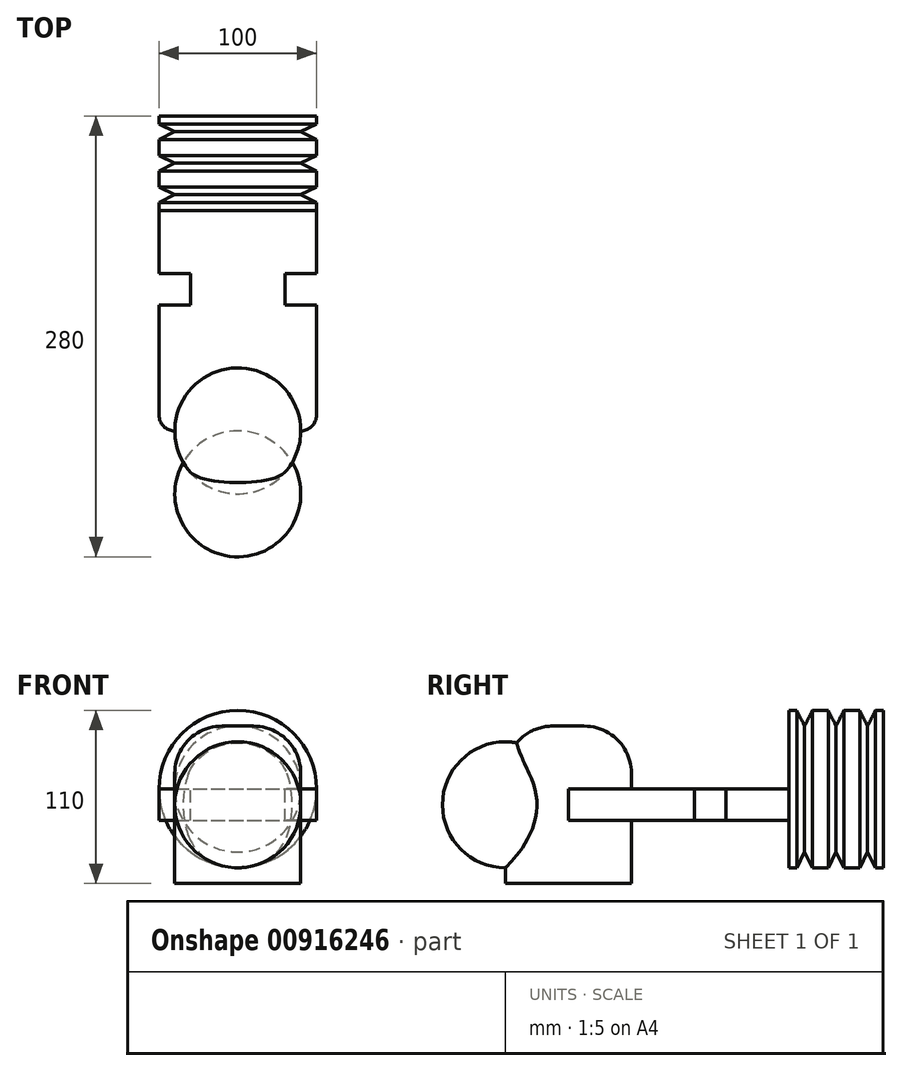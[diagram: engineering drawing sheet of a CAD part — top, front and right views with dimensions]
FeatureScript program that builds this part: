
annotation { "Feature Type Name" : "Feature", "Feature Type Description" : "" }
export const myFeature = defineFeature(function(context is Context, id is Id, definition is map)
    precondition{}
    {
        {
            var Q0;
            Q0=qCreatedBy(makeId("Front.planeOp"),FACE);
            var sketch = newSketch(context, id + "F0", { "sketchPlane" : qUnion([Q0])});
            skLineSegment(sketch, "E0.bottom", {"start": v(50, 10) * mm, "end": v(-50, 10) * mm});
            skLineSegment(sketch, "E0.top", {"start": v(50, -10) * mm, "end": v(-50, -10) * mm});
            skLineSegment(sketch, "E0.left", {"start": v(50, 10) * mm, "end": v(50, -10) * mm});
            skLineSegment(sketch, "E0.right", {"start": v(-50, 10) * mm, "end": v(-50, -10) * mm});
            skPoint(sketch, "E0.middle", {"position": v(0, 0) * mm});
            skSolve(sketch);
        }
        {
            var Q0;
            Q0 = qSketchRegion(id + "F0", true);
            extrude(context, id + "F1", {"entities" : qUnion([Q0]), "endBound" : BoundingType.SYMMETRIC, "depth" : 200 * mm, "offsetDistance" : 25 * mm});
        }
        {
            var Q0;
            Q0=makeQuery(id+"F1.opExtrude","SWEPT_FACE",FACE,{"disambiguationData":[OSD([sQuery(id+"F0.wireOp",EDGE,"E0.bottom")])]});
            var sketch = newSketch(context, id + "F2", { "sketchPlane" : qUnion([Q0])});
            skLineSegment(sketch, "E1.bottom", {"start": v(50, 0) * mm, "end": v(30, 0) * mm});
            skLineSegment(sketch, "E1.top", {"start": v(50, -20) * mm, "end": v(30, -20) * mm});
            skLineSegment(sketch, "E1.left", {"start": v(50, 0) * mm, "end": v(50, -20) * mm});
            skLineSegment(sketch, "E1.right", {"start": v(30, 0) * mm, "end": v(30, -20) * mm});
            skLineSegment(sketch, "E2.MirrorCS", {"start": v(-30, 0) * mm, "end": v(-30, -20) * mm});
            skLineSegment(sketch, "E3.MirrorCS", {"start": v(-50, 0) * mm, "end": v(-30, 0) * mm});
            skLineSegment(sketch, "E4.MirrorCS", {"start": v(-50, -20) * mm, "end": v(-30, -20) * mm});
            skLineSegment(sketch, "E5.MirrorCS", {"start": v(-50, 0) * mm, "end": v(-50, -20) * mm});
            skSolve(sketch);
        }
        {
            var Q0;
            Q0 = qSketchRegion(id + "F2", true);
            extrude(context, id + "F3", {"entities" : qUnion([Q0]), "operationType" : NewBodyOperationType.REMOVE, "oppositeDirection" : true, "depth" : 20 * mm, "offsetDistance" : 25 * mm});
        }
        {
            var Q0;
            Q0=makeQuery(id+"F1.opExtrude","SWEPT_FACE",FACE,{"disambiguationData":[OSD([sQuery(id+"F0.wireOp",EDGE,"E0.bottom")])]});
            var sketch = newSketch(context, id + "F4", { "sketchPlane" : qUnion([Q0])});
            skLineSegment(sketch, "E6", {"start": v(50, 90) * mm, "end": v(40, 90) * mm, "construction": true});
            skLineSegment(sketch, "E7", {"start": v(40, 90) * mm, "end": v(50, 95) * mm});
            skLineSegment(sketch, "E8.MirrorCS", {"start": v(40, 90) * mm, "end": v(50, 85) * mm});
            skLineSegment(sketch, "E9.1.0.0", {"start": v(40, 70) * mm, "end": v(50, 75) * mm});
            skLineSegment(sketch, "E9.1.0.1", {"start": v(40, 70) * mm, "end": v(50, 65) * mm});
            skLineSegment(sketch, "E9.2.0.0", {"start": v(40, 50) * mm, "end": v(50, 55) * mm});
            skLineSegment(sketch, "E9.2.0.1", {"start": v(40, 50) * mm, "end": v(50, 45) * mm});
            skLineSegment(sketch, "E9.direction1", {"start": v(40, 90) * mm, "end": v(40, 70) * mm, "construction": true});
            skLineSegment(sketch, "E10", {"start": v(50, 95) * mm, "end": v(50, 100) * mm});
            skLineSegment(sketch, "E11", {"start": v(50, 100) * mm, "end": v(0, 100) * mm});
            skLineSegment(sketch, "E12", {"start": v(0, 100) * mm, "end": v(0, 40) * mm});
            skLineSegment(sketch, "E13", {"start": v(0, 40) * mm, "end": v(50, 40) * mm});
            skLineSegment(sketch, "E14", {"start": v(50, 40) * mm, "end": v(50, 45) * mm});
            skLineSegment(sketch, "E15.trimOffspring", {"start": v(50, 75) * mm, "end": v(50, 85) * mm});
            skLineSegment(sketch, "E16.trimOffspring", {"start": v(50, 55) * mm, "end": v(50, 65) * mm});
            skSolve(sketch);
        }
        {
            var Q0;
            Q0 = qSketchRegion(id + "F4", true);
            var Q1;
            Q1=sQuery(id+"F4.wireOp",EDGE,"E12");
            revolve(context, id + "F5", {"surfaceOperationType" : NewSurfaceOperationType.NEW, "entities" : qUnion([Q0]), "axis" : qUnion([Q1]), "revolveType" : RevolveType.FULL});
        }
        {
            var Q0;
            Q0=makeQuery(id+"F5.opRevolve","SWEPT_BODY",BODY,{"disambiguationData":[OSD([sQuery(id+"F4.wireOp",EDGE,"E7"),sQuery(id+"F4.wireOp",EDGE,"E8.MirrorCS"),sQuery(id+"F4.wireOp",EDGE,"E9.1.0.0"),sQuery(id+"F4.wireOp",EDGE,"E9.1.0.1"),sQuery(id+"F4.wireOp",EDGE,"E9.2.0.0"),sQuery(id+"F4.wireOp",EDGE,"E9.2.0.1"),sQuery(id+"F4.wireOp",EDGE,"E11"),sQuery(id+"F4.wireOp",EDGE,"E12"),sQuery(id+"F4.wireOp",EDGE,"E13"),sQuery(id+"F4.wireOp",EDGE,"E14"),sQuery(id+"F4.wireOp",EDGE,"E10"),sQuery(id+"F4.wireOp",EDGE,"E15.trimOffspring"),sQuery(id+"F4.wireOp",EDGE,"E16.trimOffspring")])]});
            var Q1;
            Q1=makeQuery(id+"F1.opExtrude","SWEPT_BODY",BODY,{"disambiguationData":[OSD([sQuery(id+"F0.wireOp",EDGE,"E0.bottom"),sQuery(id+"F0.wireOp",EDGE,"E0.top"),sQuery(id+"F0.wireOp",EDGE,"E0.left"),sQuery(id+"F0.wireOp",EDGE,"E0.right")])]});
            booleanBodies(context, id + "F6", {"operationType" : BooleanOperationType.SUBTRACTION, "tools" : qUnion([Q0]), "targets" : qUnion([Q1]), "keepTools" : true});
        }
        {
            var Q0;
            Q0=makeQuery(id+"F1.opExtrude","CAP_EDGE",EDGE,{"disambiguationData":[OSD([sQuery(id+"F0.wireOp",EDGE,"E0.left")])],"isStart":false});
            var Q1;
            Q1=makeQuery(id+"F1.opExtrude","CAP_EDGE",EDGE,{"disambiguationData":[OSD([sQuery(id+"F0.wireOp",EDGE,"E0.right")])],"isStart":false});
            fillet(context, id + "F7", {"entities" : qUnion([Q0, Q1]), "radius" : 10 * mm, "tangentPropagation" : true, "allowEdgeOverflow" : false});
        }
        {
            var Q0;
            {var subQ0=sQuery(id+"F0.wireOp",EDGE,"E0.right");var subQ1=sQuery(id+"F0.wireOp",EDGE,"E0.left");var subQ2=sQuery(id+"F0.wireOp",EDGE,"E0.bottom");Q0=makeQuery(id+"F6.opBoolean","SPLIT",FACE,{"disambiguationData":[TD([makeQuery(id+"F1.opExtrude","CAP_FACE",FACE,{"disambiguationData":[OSD([subQ2,sQuery(id+"F0.wireOp",EDGE,"E0.top"),subQ1,subQ0])],"isStart":false}),makeQuery(id+"F1.opExtrude","SWEPT_FACE",FACE,{"disambiguationData":[OSD([subQ1])]}),makeQuery(id+"F1.opExtrude","SWEPT_FACE",FACE,{"disambiguationData":[OSD([subQ0])]}),makeQuery(id+"F3.boolean.opBoolean","COPY",FACE,{"derivedFrom":makeQuery(id+"F3.opExtrude","SWEPT_FACE",FACE,{"disambiguationData":[OSD([sQuery(id+"F2.wireOp",EDGE,"E1.bottom")])]})}),makeQuery(id+"F3.boolean.opBoolean","COPY",FACE,{"derivedFrom":makeQuery(id+"F3.opExtrude","SWEPT_FACE",FACE,{"disambiguationData":[OSD([sQuery(id+"F2.wireOp",EDGE,"E1.top")])]})}),makeQuery(id+"F3.boolean.opBoolean","COPY",FACE,{"derivedFrom":makeQuery(id+"F3.opExtrude","SWEPT_FACE",FACE,{"disambiguationData":[OSD([sQuery(id+"F2.wireOp",EDGE,"E1.right")])]})}),makeQuery(id+"F3.boolean.opBoolean","COPY",FACE,{"derivedFrom":makeQuery(id+"F3.opExtrude","SWEPT_FACE",FACE,{"disambiguationData":[OSD([sQuery(id+"F2.wireOp",EDGE,"E2.MirrorCS")])]})}),makeQuery(id+"F3.boolean.opBoolean","COPY",FACE,{"derivedFrom":makeQuery(id+"F3.opExtrude","SWEPT_FACE",FACE,{"disambiguationData":[OSD([sQuery(id+"F2.wireOp",EDGE,"E3.MirrorCS")])]})}),makeQuery(id+"F3.boolean.opBoolean","COPY",FACE,{"derivedFrom":makeQuery(id+"F3.opExtrude","SWEPT_FACE",FACE,{"disambiguationData":[OSD([sQuery(id+"F2.wireOp",EDGE,"E4.MirrorCS")])]})}),makeQuery(id+"F5.opRevolve","SWEPT_FACE",FACE,{"disambiguationData":[OSD([sQuery(id+"F4.wireOp",EDGE,"E13")])]}),makeQuery(id+"F5.opRevolve","SWEPT_FACE",FACE,{"disambiguationData":[OSD([sQuery(id+"F4.wireOp",EDGE,"E14")])]})])],"derivedFrom":makeQuery(id+"F1.opExtrude","SWEPT_FACE",FACE,{"disambiguationData":[OSD([subQ2])]})});}
            var sketch = newSketch(context, id + "F8", { "sketchPlane" : qUnion([Q0])});
            skCircle(sketch, "E17", {"center": v(0, -120) * mm, "radius": 20 * mm});
            skPoint(sketch, "E17.centerSnap0", {"position": v(0, -100) * mm});
            skLineSegment(sketch, "E18", {"start": v(0, -100) * mm, "end": v(0, -140) * mm});
            skSolve(sketch);
        }
        {
            var Q0;
            Q0=makeQuery(id+"F6.opBoolean","COPY",FACE,{"derivedFrom":makeQuery(id+"F5.opRevolve","SWEPT_FACE",FACE,{"disambiguationData":[OSD([sQuery(id+"F4.wireOp",EDGE,"E13")])]})});
            var sketch = newSketch(context, id + "F9", { "sketchPlane" : qUnion([Q0])});
            skCircle(sketch, "E19", {"center": v(0, 0) * mm, "radius": 60 * mm});
            skSolve(sketch);
        }
        {
            var Q0;
            Q0 = qSketchRegion(id + "F9", true);
            extrude(context, id + "F10", {"entities" : qUnion([Q0]), "depth" : 60 * mm, "offsetDistance" : 25 * mm});
        }
        {
            var Q0;
            Q0=makeQuery(id+"F10.opExtrude","SWEPT_BODY",BODY,{"disambiguationData":[OSD([sQuery(id+"F9.wireOp",EDGE,"E19")])]});
            var Q1;
            Q1=makeQuery(id+"F1.opExtrude","SWEPT_BODY",BODY,{"disambiguationData":[OSD([sQuery(id+"F0.wireOp",EDGE,"E0.bottom"),sQuery(id+"F0.wireOp",EDGE,"E0.top"),sQuery(id+"F0.wireOp",EDGE,"E0.left"),sQuery(id+"F0.wireOp",EDGE,"E0.right")])]});
            booleanBodies(context, id + "F11", {"operationType" : BooleanOperationType.SUBTRACTION, "tools" : qUnion([Q0]), "targets" : qUnion([Q1])});
        }
        {
            var Q0;
            Q0 = qSketchRegion(id + "F8", true);
            extrude(context, id + "F12", {"entities" : qUnion([Q0]), "oppositeDirection" : true, "depth" : 20 * mm, "offsetDistance" : 25 * mm});
        }
        {
            var Q0;
            Q0=makeQuery(id+"F12.opExtrude","SWEPT_BODY",BODY,{"disambiguationData":[OSD([sQuery(id+"F8.wireOp",EDGE,"E17")])]});
            deleteBodies(context, id + "F13", {"entities" : qUnion([Q0])});
        }
        {
            var Q0;
            Q0=qCreatedBy(makeId("Top.planeOp"),FACE);
            var sketch = newSketch(context, id + "F14", { "sketchPlane" : qUnion([Q0])});
            skCircle(sketch, "E20", {"center": v(0, -140) * mm, "radius": 40 * mm});
            skLineSegment(sketch, "E21", {"start": v(0, -180) * mm, "end": v(0, -100) * mm, "construction": true});
            skSolve(sketch);
        }
        {
            var Q0;
            Q0=makeQuery(id+"F14.imprint","IMPRINT",FACE,{"disambiguationData":[TD([[makeQuery(id+"F14.imprint","IMPRINT",EDGE,{"derivedFrom":sQuery(id+"F14.wireOp",EDGE,"E20")}),1.0]])]});
            extrude(context, id + "F15", {"entities" : qUnion([Q0]), "depth" : 40 * mm, "offsetDistance" : 25 * mm});
        }
        {
            var Q0;
            Q0=makeQuery(id+"F15.opExtrude","CAP_EDGE",EDGE,{"disambiguationData":[OSD([sQuery(id+"F14.wireOp",EDGE,"E20")])],"isStart":false});
            fillet(context, id + "F16", {"entities" : qUnion([Q0]), "radius" : 40 * mm, "tangentPropagation" : true, "allowEdgeOverflow" : false});
        }
        {
            var Q0;
            Q0=makeQuery(id+"F15.opExtrude","SWEPT_BODY",BODY,{"disambiguationData":[OSD([sQuery(id+"F14.wireOp",EDGE,"E20")])]});
            var Q1;
            Q1=qCreatedBy(makeId("Top.planeOp"),FACE);
            mirror(context, id + "F17", {"operationType" : NewBodyOperationType.ADD, "entities" : qUnion([Q0]), "mirrorPlane" : qUnion([Q1])});
        }
        {
            var Q0;
            {var subQ0=sQuery(id+"F0.wireOp",EDGE,"E0.right");var subQ1=sQuery(id+"F0.wireOp",EDGE,"E0.left");var subQ2=sQuery(id+"F0.wireOp",EDGE,"E0.bottom");Q0=makeQuery(id+"F6.opBoolean","SPLIT",FACE,{"disambiguationData":[TD([makeQuery(id+"F1.opExtrude","CAP_FACE",FACE,{"disambiguationData":[OSD([subQ2,sQuery(id+"F0.wireOp",EDGE,"E0.top"),subQ1,subQ0])],"isStart":false}),makeQuery(id+"F1.opExtrude","SWEPT_FACE",FACE,{"disambiguationData":[OSD([subQ1])]}),makeQuery(id+"F1.opExtrude","SWEPT_FACE",FACE,{"disambiguationData":[OSD([subQ0])]}),makeQuery(id+"F3.boolean.opBoolean","COPY",FACE,{"derivedFrom":makeQuery(id+"F3.opExtrude","SWEPT_FACE",FACE,{"disambiguationData":[OSD([sQuery(id+"F2.wireOp",EDGE,"E1.bottom")])]})}),makeQuery(id+"F3.boolean.opBoolean","COPY",FACE,{"derivedFrom":makeQuery(id+"F3.opExtrude","SWEPT_FACE",FACE,{"disambiguationData":[OSD([sQuery(id+"F2.wireOp",EDGE,"E1.top")])]})}),makeQuery(id+"F3.boolean.opBoolean","COPY",FACE,{"derivedFrom":makeQuery(id+"F3.opExtrude","SWEPT_FACE",FACE,{"disambiguationData":[OSD([sQuery(id+"F2.wireOp",EDGE,"E1.right")])]})}),makeQuery(id+"F3.boolean.opBoolean","COPY",FACE,{"derivedFrom":makeQuery(id+"F3.opExtrude","SWEPT_FACE",FACE,{"disambiguationData":[OSD([sQuery(id+"F2.wireOp",EDGE,"E2.MirrorCS")])]})}),makeQuery(id+"F3.boolean.opBoolean","COPY",FACE,{"derivedFrom":makeQuery(id+"F3.opExtrude","SWEPT_FACE",FACE,{"disambiguationData":[OSD([sQuery(id+"F2.wireOp",EDGE,"E3.MirrorCS")])]})}),makeQuery(id+"F3.boolean.opBoolean","COPY",FACE,{"derivedFrom":makeQuery(id+"F3.opExtrude","SWEPT_FACE",FACE,{"disambiguationData":[OSD([sQuery(id+"F2.wireOp",EDGE,"E4.MirrorCS")])]})}),makeQuery(id+"F5.opRevolve","SWEPT_FACE",FACE,{"disambiguationData":[OSD([sQuery(id+"F4.wireOp",EDGE,"E13")])]}),makeQuery(id+"F5.opRevolve","SWEPT_FACE",FACE,{"disambiguationData":[OSD([sQuery(id+"F4.wireOp",EDGE,"E14")])]})])],"derivedFrom":makeQuery(id+"F1.opExtrude","SWEPT_FACE",FACE,{"disambiguationData":[OSD([subQ2])]})});}
            var sketch = newSketch(context, id + "F18", { "sketchPlane" : qUnion([Q0])});
            skCircle(sketch, "E22", {"center": v(0, -100) * mm, "radius": 40 * mm});
            skSolve(sketch);
        }
        {
            var Q0;
            Q0 = qSketchRegion(id + "F18", true);
            extrude(context, id + "F19", {"entities" : qUnion([Q0]), "depth" : 40 * mm, "offsetDistance" : 25 * mm});
        }
        {
            var Q0;
            Q0=makeQuery(id+"F19.opExtrude","CAP_EDGE",EDGE,{"disambiguationData":[OSD([sQuery(id+"F18.wireOp",EDGE,"E22")])],"isStart":false});
            fillet(context, id + "F20", {"entities" : qUnion([Q0]), "radius" : 30 * mm, "tangentPropagation" : true, "allowEdgeOverflow" : false});
        }
        {
            var Q0;
            Q0=makeQuery(id+"F19.opExtrude","SWEPT_BODY",BODY,{"disambiguationData":[OSD([sQuery(id+"F18.wireOp",EDGE,"E22")])]});
            var Q1;
            Q1=makeQuery(id+"F1.opExtrude","SWEPT_BODY",BODY,{"disambiguationData":[OSD([sQuery(id+"F0.wireOp",EDGE,"E0.bottom"),sQuery(id+"F0.wireOp",EDGE,"E0.top"),sQuery(id+"F0.wireOp",EDGE,"E0.left"),sQuery(id+"F0.wireOp",EDGE,"E0.right")])]});
            booleanBodies(context, id + "F21", {"operationType" : BooleanOperationType.SUBTRACTION, "tools" : qUnion([Q0]), "targets" : qUnion([Q1]), "keepTools" : true});
        }
        {
            var Q0;
            Q0=makeQuery(id+"F19.opExtrude","CAP_FACE",FACE,{"disambiguationData":[OSD([sQuery(id+"F18.wireOp",EDGE,"E22")])],"isStart":true});
            extrude(context, id + "F22", {"entities" : qUnion([Q0]), "operationType" : NewBodyOperationType.ADD, "depth" : 60 * mm, "offsetDistance" : 25 * mm});
        }
    });
